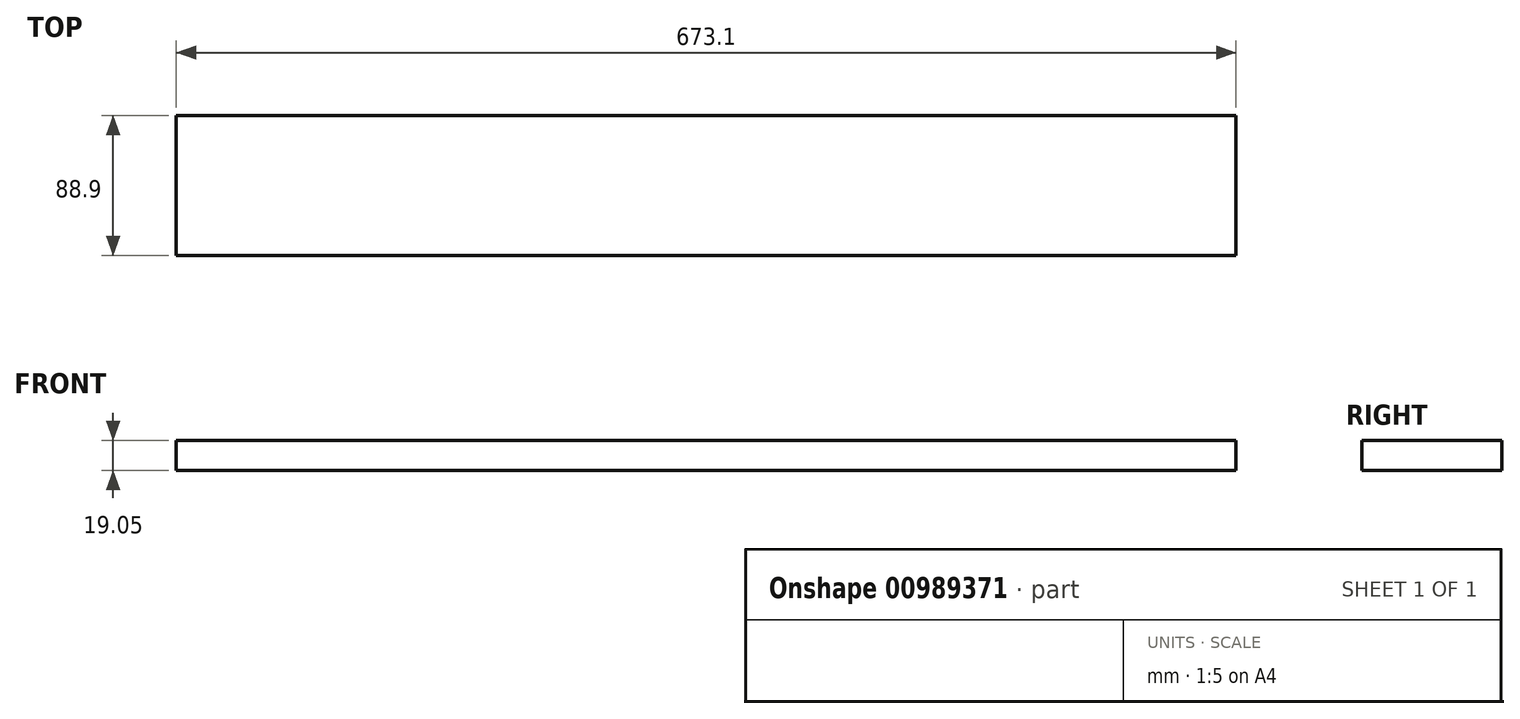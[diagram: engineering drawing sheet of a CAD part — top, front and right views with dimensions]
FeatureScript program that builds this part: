
annotation { "Feature Type Name" : "Feature", "Feature Type Description" : "" }
export const myFeature = defineFeature(function(context is Context, id is Id, definition is map)
    precondition{}
    {
        {
            var Q0;
            Q0=qCreatedBy(makeId("Right.planeOp"),FACE);
            var sketch = newSketch(context, id + "F0", { "sketchPlane" : qUnion([Q0])});
            skLineSegment(sketch, "E0.bottom", {"start": v(-63.5, 13.63) * mm, "end": v(25.4, 13.63) * mm});
            skLineSegment(sketch, "E0.top", {"start": v(-63.5, -5.42) * mm, "end": v(25.4, -5.42) * mm});
            skLineSegment(sketch, "E0.left", {"start": v(-63.5, 13.63) * mm, "end": v(-63.5, -5.42) * mm});
            skLineSegment(sketch, "E0.right", {"start": v(25.4, 13.63) * mm, "end": v(25.4, -5.42) * mm});
            skSolve(sketch);
        }
        {
            var Q0;
            Q0=makeQuery(id+"F0.imprint","IMPRINT",FACE,{"disambiguationData":[TD([[makeQuery(id+"F0.imprint","IMPRINT",EDGE,{"derivedFrom":sQuery(id+"F0.wireOp",EDGE,"E0.bottom")}),-1.0]])]});
            extrude(context, id + "F1", {"entities" : qUnion([Q0]), "depth" : 673.1 * mm, "offsetDistance" : 25.4 * mm});
        }
    });
